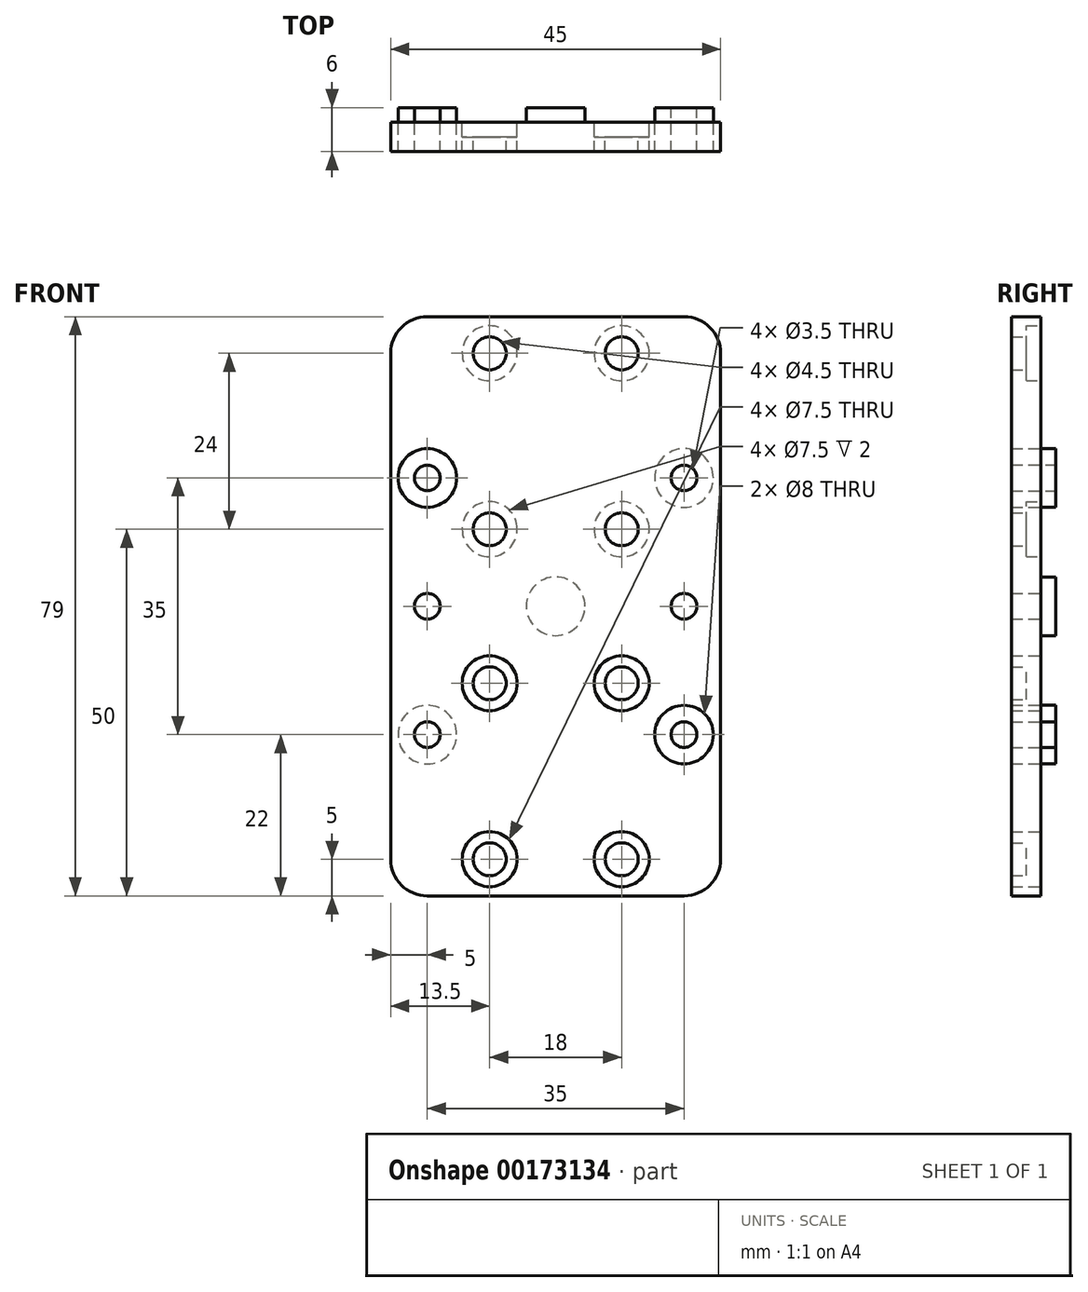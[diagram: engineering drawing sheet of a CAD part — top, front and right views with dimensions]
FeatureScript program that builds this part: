
annotation { "Feature Type Name" : "Feature", "Feature Type Description" : "" }
export const myFeature = defineFeature(function(context is Context, id is Id, definition is map)
    precondition{}
    {
        {
            var Q0;
            Q0=qCreatedBy(makeId("Front.planeOp"),FACE);
            var sketch = newSketch(context, id + "F0", { "sketchPlane" : qUnion([Q0])});
            skLineSegment(sketch, "E0.bottom", {"start": v(-22.5, 39.5) * mm, "end": v(22.5, 39.5) * mm});
            skLineSegment(sketch, "E0.top", {"start": v(-22.5, -39.5) * mm, "end": v(22.5, -39.5) * mm});
            skLineSegment(sketch, "E0.left", {"start": v(-22.5, 39.5) * mm, "end": v(-22.5, -39.5) * mm});
            skLineSegment(sketch, "E0.right", {"start": v(22.5, 39.5) * mm, "end": v(22.5, -39.5) * mm});
            skPoint(sketch, "E1", {"position": v(-9, 34.5) * mm});
            skPoint(sketch, "E2", {"position": v(9, 34.5) * mm});
            skPoint(sketch, "E3", {"position": v(9, 10.5) * mm});
            skPoint(sketch, "E4", {"position": v(-9, 10.5) * mm});
            skCircle(sketch, "E5", {"center": v(-9, 34.5) * mm, "radius": 2.25 * mm});
            skCircle(sketch, "E6", {"center": v(9, 34.5) * mm, "radius": 2.25 * mm});
            skCircle(sketch, "E7", {"center": v(9, 10.5) * mm, "radius": 2.25 * mm});
            skCircle(sketch, "E8", {"center": v(-9, 10.5) * mm, "radius": 2.25 * mm});
            skCircle(sketch, "E9.MirrorC", {"center": v(-9, -10.5) * mm, "radius": 2.25 * mm});
            skCircle(sketch, "E10.MirrorC", {"center": v(9, -10.5) * mm, "radius": 2.25 * mm});
            skCircle(sketch, "E11.MirrorC", {"center": v(9, -34.5) * mm, "radius": 2.25 * mm});
            skCircle(sketch, "E12.MirrorC", {"center": v(-9, -34.5) * mm, "radius": 2.25 * mm});
            skLineSegment(sketch, "E13", {"start": v(-9, 10.5) * mm, "end": v(9, 34.5) * mm});
            skLineSegment(sketch, "E14", {"start": v(-9, 34.5) * mm, "end": v(9, 10.5) * mm});
            skPoint(sketch, "E15", {"position": v(0, 22.5) * mm});
            skCircle(sketch, "E16", {"center": v(17.5, 17.5) * mm, "radius": 1.75 * mm});
            skCircle(sketch, "E17.MirrorC", {"center": v(-17.5, 17.5) * mm, "radius": 1.75 * mm});
            skCircle(sketch, "E18.MirrorC", {"center": v(-17.5, -17.5) * mm, "radius": 1.75 * mm});
            skCircle(sketch, "E19.MirrorC", {"center": v(17.5, -17.5) * mm, "radius": 1.75 * mm});
            skCircle(sketch, "E20.MirrorC", {"center": v(-17.5, 0) * mm, "radius": 1.75 * mm});
            skCircle(sketch, "E21.MirrorC", {"center": v(17.5, 0) * mm, "radius": 1.75 * mm});
            skCircle(sketch, "E22", {"center": v(-17.5, 17.5) * mm, "radius": 4 * mm});
            skCircle(sketch, "E23.MirrorC", {"center": v(17.5, 17.5) * mm, "radius": 4 * mm});
            skCircle(sketch, "E24.MirrorC", {"center": v(17.5, -17.5) * mm, "radius": 4 * mm});
            skCircle(sketch, "E25.MirrorC", {"center": v(-17.5, -17.5) * mm, "radius": 4 * mm});
            skCircle(sketch, "E26", {"center": v(0, 0) * mm, "radius": 4 * mm});
            skCircle(sketch, "E27", {"center": v(-9, 34.5) * mm, "radius": 3.75 * mm});
            skCircle(sketch, "E28.MirrorC", {"center": v(9, 34.5) * mm, "radius": 3.75 * mm});
            skCircle(sketch, "E29.MirrorC", {"center": v(9, 10.5) * mm, "radius": 3.75 * mm});
            skCircle(sketch, "E30.MirrorC", {"center": v(-9, 10.5) * mm, "radius": 3.75 * mm});
            skCircle(sketch, "E31.MirrorC", {"center": v(9, -10.5) * mm, "radius": 3.75 * mm});
            skCircle(sketch, "E32.MirrorC", {"center": v(-9, -10.5) * mm, "radius": 3.75 * mm});
            skCircle(sketch, "E33.MirrorC", {"center": v(-9, -34.5) * mm, "radius": 3.75 * mm});
            skCircle(sketch, "E34.MirrorC", {"center": v(9, -34.5) * mm, "radius": 3.75 * mm});
            skSolve(sketch);
        }
        {
            var Q0;
            Q0 = qSketchRegion(id + "F0", true);
            var Q1;
            Q1=makeQuery(id+"F0.imprint","IMPRINT",FACE,{"disambiguationData":[TD([[makeQuery(id+"F0.imprint","IMPRINT",EDGE,{"derivedFrom":sQuery(id+"F0.wireOp",EDGE,"E17.MirrorC")}),1.0]])]});
            var Q2;
            Q2=makeQuery(id+"F0.imprint","IMPRINT",FACE,{"disambiguationData":[TD([[makeQuery(id+"F0.imprint","IMPRINT",EDGE,{"derivedFrom":sQuery(id+"F0.wireOp",EDGE,"E26")}),1.0]])]});
            var Q3;
            Q3=makeQuery(id+"F0.imprint","IMPRINT",FACE,{"disambiguationData":[TD([[makeQuery(id+"F0.imprint","IMPRINT",EDGE,{"derivedFrom":sQuery(id+"F0.wireOp",EDGE,"E18.MirrorC")}),-1.0]])]});
            var Q4;
            Q4=makeQuery(id+"F0.imprint","IMPRINT",FACE,{"disambiguationData":[TD([[makeQuery(id+"F0.imprint","IMPRINT",EDGE,{"derivedFrom":sQuery(id+"F0.wireOp",EDGE,"E19.MirrorC")}),1.0]])]});
            var Q5;
            Q5=makeQuery(id+"F0.imprint","IMPRINT",FACE,{"disambiguationData":[TD([[makeQuery(id+"F0.imprint","IMPRINT",EDGE,{"derivedFrom":sQuery(id+"F0.wireOp",EDGE,"E16")}),-1.0]])]});
            var Q6;
            Q6=makeQuery(id+"F0.imprint","IMPRINT",FACE,{"disambiguationData":[TD([[makeQuery(id+"F0.imprint","IMPRINT",EDGE,{"derivedFrom":sQuery(id+"F0.wireOp",EDGE,"E10.MirrorC")}),1.0]])]});
            var Q7;
            Q7=makeQuery(id+"F0.imprint","IMPRINT",FACE,{"disambiguationData":[TD([[makeQuery(id+"F0.imprint","IMPRINT",EDGE,{"derivedFrom":sQuery(id+"F0.wireOp",EDGE,"E9.MirrorC")}),1.0]])]});
            var Q8;
            Q8=makeQuery(id+"F0.imprint","IMPRINT",FACE,{"disambiguationData":[TD([[makeQuery(id+"F0.imprint","IMPRINT",EDGE,{"derivedFrom":sQuery(id+"F0.wireOp",EDGE,"E11.MirrorC")}),1.0]])]});
            var Q9;
            Q9=makeQuery(id+"F0.imprint","IMPRINT",FACE,{"disambiguationData":[TD([[makeQuery(id+"F0.imprint","IMPRINT",EDGE,{"derivedFrom":sQuery(id+"F0.wireOp",EDGE,"E12.MirrorC")}),1.0]])]});
            var Q10;
            Q10=makeQuery(id+"F0.imprint","IMPRINT",FACE,{"disambiguationData":[TD([[makeQuery(id+"F0.imprint","IMPRINT",EDGE,{"derivedFrom":sQuery(id+"F0.wireOp",EDGE,"E7")}),-1.0]])]});
            var Q11;
            Q11=makeQuery(id+"F0.imprint","IMPRINT",FACE,{"disambiguationData":[TD([[makeQuery(id+"F0.imprint","IMPRINT",EDGE,{"derivedFrom":sQuery(id+"F0.wireOp",EDGE,"E8")}),-1.0]])]});
            var Q12;
            Q12=makeQuery(id+"F0.imprint","IMPRINT",FACE,{"disambiguationData":[TD([[makeQuery(id+"F0.imprint","IMPRINT",EDGE,{"derivedFrom":sQuery(id+"F0.wireOp",EDGE,"E6")}),-1.0]])]});
            var Q13;
            Q13=makeQuery(id+"F0.imprint","IMPRINT",FACE,{"disambiguationData":[TD([[makeQuery(id+"F0.imprint","IMPRINT",EDGE,{"derivedFrom":sQuery(id+"F0.wireOp",EDGE,"E5")}),-1.0]])]});
            extrude(context, id + "F1", {"entities" : qUnion([Q0, Q1, Q2, Q3, Q4, Q5, Q6, Q7, Q8, Q9, Q10, Q11, Q12, Q13]), "depth" : 4 * mm});
        }
        {
            var Q0;
            Q0=makeQuery(id+"F0.imprint","IMPRINT",FACE,{"disambiguationData":[TD([[makeQuery(id+"F0.imprint","IMPRINT",EDGE,{"derivedFrom":sQuery(id+"F0.wireOp",EDGE,"E17.MirrorC")}),1.0]])]});
            var Q1;
            Q1=makeQuery(id+"F0.imprint","IMPRINT",FACE,{"disambiguationData":[TD([[makeQuery(id+"F0.imprint","IMPRINT",EDGE,{"derivedFrom":sQuery(id+"F0.wireOp",EDGE,"E16")}),-1.0]])]});
            var Q2;
            Q2=makeQuery(id+"F0.imprint","IMPRINT",FACE,{"disambiguationData":[TD([[makeQuery(id+"F0.imprint","IMPRINT",EDGE,{"derivedFrom":sQuery(id+"F0.wireOp",EDGE,"E26")}),1.0]])]});
            var Q3;
            Q3=makeQuery(id+"F0.imprint","IMPRINT",FACE,{"disambiguationData":[TD([[makeQuery(id+"F0.imprint","IMPRINT",EDGE,{"derivedFrom":sQuery(id+"F0.wireOp",EDGE,"E18.MirrorC")}),-1.0]])]});
            var Q4;
            Q4=makeQuery(id+"F0.imprint","IMPRINT",FACE,{"disambiguationData":[TD([[makeQuery(id+"F0.imprint","IMPRINT",EDGE,{"derivedFrom":sQuery(id+"F0.wireOp",EDGE,"E19.MirrorC")}),1.0]])]});
            extrude(context, id + "F2", {"entities" : qUnion([Q0, Q1, Q2, Q3, Q4]), "operationType" : NewBodyOperationType.ADD, "oppositeDirection" : true, "depth" : 2 * mm});
        }
        {
            var Q0;
            Q0=makeQuery(id+"F1.opExtrude","SWEPT_EDGE",EDGE,{"disambiguationData":[OSD([sQuery(id+"F0.wireOp",EDGE,"E0.bottom"),sQuery(id+"F0.wireOp",EDGE,"E0.left")])]});
            var Q1;
            Q1=makeQuery(id+"F1.opExtrude","SWEPT_EDGE",EDGE,{"disambiguationData":[OSD([sQuery(id+"F0.wireOp",EDGE,"E0.top"),sQuery(id+"F0.wireOp",EDGE,"E0.left")])]});
            var Q2;
            Q2=makeQuery(id+"F1.opExtrude","SWEPT_EDGE",EDGE,{"disambiguationData":[OSD([sQuery(id+"F0.wireOp",EDGE,"E0.top"),sQuery(id+"F0.wireOp",EDGE,"E0.right")])]});
            var Q3;
            Q3=makeQuery(id+"F1.opExtrude","SWEPT_EDGE",EDGE,{"disambiguationData":[OSD([sQuery(id+"F0.wireOp",EDGE,"E0.bottom"),sQuery(id+"F0.wireOp",EDGE,"E0.right")])]});
            fillet(context, id + "F3", {"entities" : qUnion([Q0, Q1, Q2, Q3]), "radius" : 5 * mm, "tangentPropagation" : true, "allowEdgeOverflow" : false});
        }
        {
            var Q0;
            Q0=makeQuery(id+"F0.imprint","IMPRINT",FACE,{"disambiguationData":[TD([[makeQuery(id+"F0.imprint","IMPRINT",EDGE,{"derivedFrom":sQuery(id+"F0.wireOp",EDGE,"E5")}),-1.0]])]});
            var Q1;
            Q1=makeQuery(id+"F0.imprint","IMPRINT",FACE,{"disambiguationData":[TD([[makeQuery(id+"F0.imprint","IMPRINT",EDGE,{"derivedFrom":sQuery(id+"F0.wireOp",EDGE,"E8")}),-1.0]])]});
            var Q2;
            Q2=makeQuery(id+"F0.imprint","IMPRINT",FACE,{"disambiguationData":[TD([[makeQuery(id+"F0.imprint","IMPRINT",EDGE,{"derivedFrom":sQuery(id+"F0.wireOp",EDGE,"E7")}),-1.0]])]});
            var Q3;
            Q3=makeQuery(id+"F0.imprint","IMPRINT",FACE,{"disambiguationData":[TD([[makeQuery(id+"F0.imprint","IMPRINT",EDGE,{"derivedFrom":sQuery(id+"F0.wireOp",EDGE,"E6")}),-1.0]])]});
            var Q4;
            Q4=makeQuery(id+"F0.imprint","IMPRINT",FACE,{"disambiguationData":[TD([[makeQuery(id+"F0.imprint","IMPRINT",EDGE,{"derivedFrom":sQuery(id+"F0.wireOp",EDGE,"E9.MirrorC")}),1.0]])]});
            var Q5;
            Q5=makeQuery(id+"F0.imprint","IMPRINT",FACE,{"disambiguationData":[TD([[makeQuery(id+"F0.imprint","IMPRINT",EDGE,{"derivedFrom":sQuery(id+"F0.wireOp",EDGE,"E10.MirrorC")}),1.0]])]});
            var Q6;
            Q6=makeQuery(id+"F0.imprint","IMPRINT",FACE,{"disambiguationData":[TD([[makeQuery(id+"F0.imprint","IMPRINT",EDGE,{"derivedFrom":sQuery(id+"F0.wireOp",EDGE,"E11.MirrorC")}),1.0]])]});
            var Q7;
            Q7=makeQuery(id+"F0.imprint","IMPRINT",FACE,{"disambiguationData":[TD([[makeQuery(id+"F0.imprint","IMPRINT",EDGE,{"derivedFrom":sQuery(id+"F0.wireOp",EDGE,"E12.MirrorC")}),1.0]])]});
            extrude(context, id + "F4", {"entities" : qUnion([Q0, Q1, Q2, Q3, Q4, Q5, Q6, Q7]), "operationType" : NewBodyOperationType.REMOVE, "depth" : 2 * mm});
        }
    });
